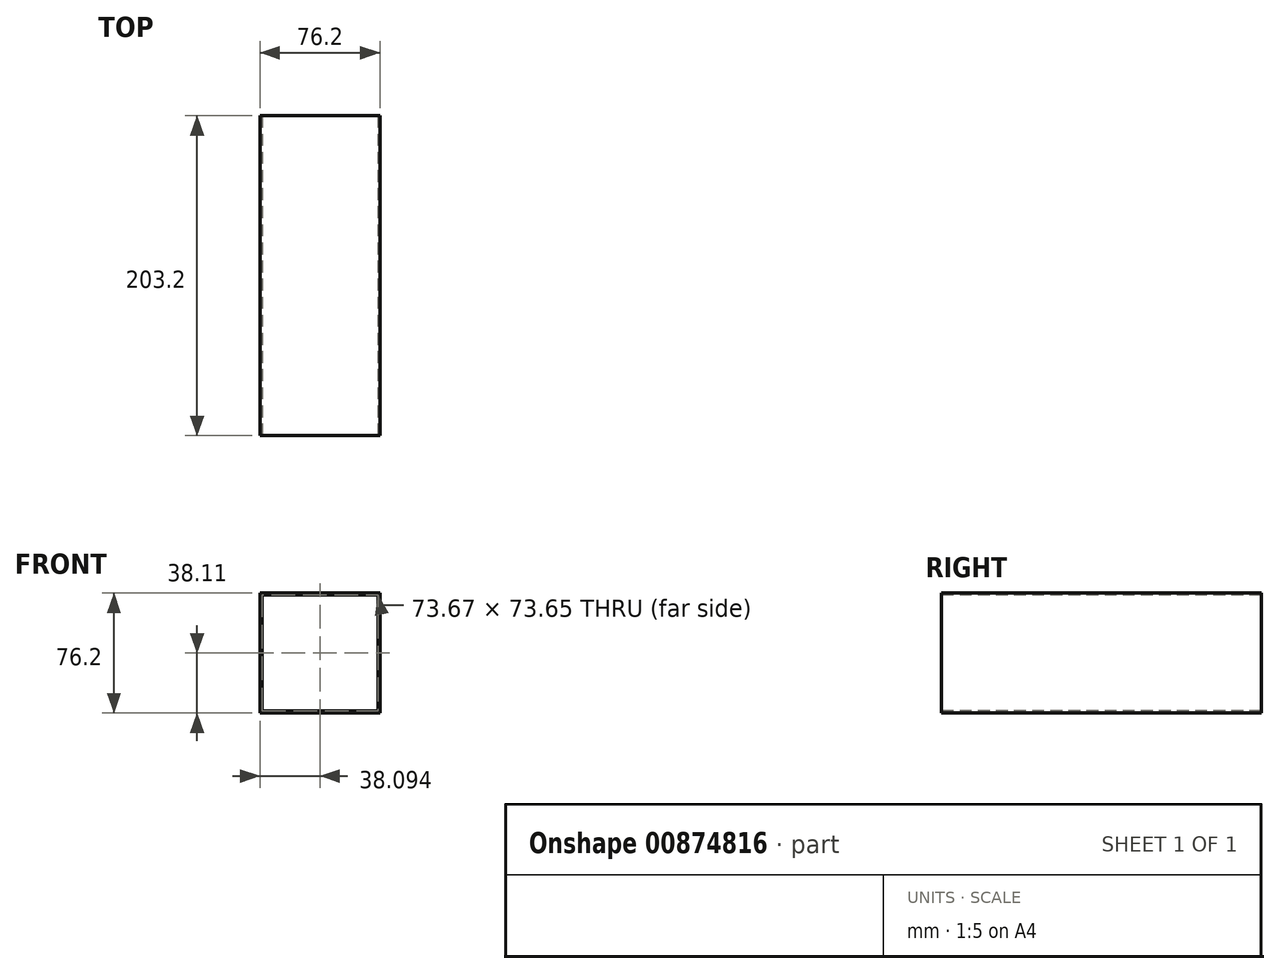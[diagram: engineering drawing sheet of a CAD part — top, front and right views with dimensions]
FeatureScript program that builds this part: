
annotation { "Feature Type Name" : "Feature", "Feature Type Description" : "" }
export const myFeature = defineFeature(function(context is Context, id is Id, definition is map)
    precondition{}
    {
        {
            var Q0;
            Q0=qCreatedBy(makeId("Front.planeOp"),FACE);
            var sketch = newSketch(context, id + "F0", { "sketchPlane" : qUnion([Q0])});
            skLineSegment(sketch, "E0.bottom", {"start": v(-117.25, 89.57) * mm, "end": v(-41.05, 89.57) * mm});
            skLineSegment(sketch, "E0.top", {"start": v(-117.25, 13.37) * mm, "end": v(-41.05, 13.37) * mm});
            skLineSegment(sketch, "E0.left", {"start": v(-117.25, 89.57) * mm, "end": v(-117.25, 13.37) * mm});
            skLineSegment(sketch, "E0.right", {"start": v(-41.05, 89.57) * mm, "end": v(-41.05, 13.37) * mm});
            skSolve(sketch);
        }
        {
            var Q0;
            Q0=qSketchRegion(id+"F0",true);
            extrude(context, id + "F1", {"entities" : qUnion([Q0]), "depth" : 609.6 * mm, "offsetDistance" : 25.4 * mm});
        }
        {
            var Q0;
            Q0=makeQuery(id+"F1.opExtrude","CAP_FACE",FACE,{"disambiguationData":[OSD([sQuery(id+"F0.wireOp",EDGE,"E0.bottom"),sQuery(id+"F0.wireOp",EDGE,"E0.top"),sQuery(id+"F0.wireOp",EDGE,"E0.left"),sQuery(id+"F0.wireOp",EDGE,"E0.right")])],"isStart":false});
            var sketch = newSketch(context, id + "F2", { "sketchPlane" : qUnion([Q0])});
            skLineSegment(sketch, "E1", {"start": v(-98.69, 89.57) * mm, "end": v(-98.69, 88.3) * mm});
            skLineSegment(sketch, "E2", {"start": v(-98.69, 88.3) * mm, "end": v(-116, 88.3) * mm});
            skLineSegment(sketch, "E3", {"start": v(-116, 88.3) * mm, "end": v(-116, 14.66) * mm});
            skLineSegment(sketch, "E4", {"start": v(-116, 14.66) * mm, "end": v(-42.32, 14.66) * mm});
            skLineSegment(sketch, "E5", {"start": v(-42.32, 14.66) * mm, "end": v(-42.32, 88.3) * mm});
            skLineSegment(sketch, "E6", {"start": v(-42.32, 88.3) * mm, "end": v(-98.69, 88.3) * mm});
            skSolve(sketch);
        }
        {
            var Q0;
            Q0=makeQuery(id+"F2.imprint","IMPRINT",FACE,{"disambiguationData":[TD([[makeQuery(id+"F2.imprint","IMPRINT",EDGE,{"derivedFrom":sQuery(id+"F2.wireOp",EDGE,"E2")}),1.0]])]});
            extrude(context, id + "F3", {"entities" : qUnion([Q0]), "operationType" : NewBodyOperationType.REMOVE, "oppositeDirection" : true, "depth" : 914.4 * mm, "offsetDistance" : 25.4 * mm});
        }
        {
            var Q0;
            Q0=makeQuery(id+"F1.opExtrude","CAP_FACE",FACE,{"disambiguationData":[OSD([sQuery(id+"F0.wireOp",EDGE,"E0.bottom"),sQuery(id+"F0.wireOp",EDGE,"E0.top"),sQuery(id+"F0.wireOp",EDGE,"E0.left"),sQuery(id+"F0.wireOp",EDGE,"E0.right")])],"isStart":false});
            extrude(context, id + "F4", {"entities" : qUnion([Q0]), "operationType" : NewBodyOperationType.ADD, "depth" : 304.8 * mm, "offsetDistance" : 25.4 * mm});
        }
        {
            var Q0;
            Q0=makeQuery(id+"F1.opExtrude","CAP_FACE",FACE,{"disambiguationData":[OSD([sQuery(id+"F0.wireOp",EDGE,"E0.bottom"),sQuery(id+"F0.wireOp",EDGE,"E0.top"),sQuery(id+"F0.wireOp",EDGE,"E0.left"),sQuery(id+"F0.wireOp",EDGE,"E0.right")])],"isStart":true});
            extrude(context, id + "F5", {"entities" : qUnion([Q0]), "operationType" : NewBodyOperationType.REMOVE, "oppositeDirection" : true, "depth" : 508 * mm, "offsetDistance" : 25.4 * mm});
        }
        {
            var Q0;
            Q0=makeQuery(id+"F5.boolean.opBoolean","COPY",FACE,{"derivedFrom":makeQuery(id+"F5.opExtrude","CAP_FACE",FACE,{"disambiguationData":[OSD([sQuery(id+"F0.wireOp",EDGE,"E0.bottom"),sQuery(id+"F0.wireOp",EDGE,"E0.top"),sQuery(id+"F0.wireOp",EDGE,"E0.left"),sQuery(id+"F0.wireOp",EDGE,"E0.right")])],"isStart":false})});
            extrude(context, id + "F6", {"entities" : qUnion([Q0]), "operationType" : NewBodyOperationType.REMOVE, "oppositeDirection" : true, "depth" : 381 * mm, "offsetDistance" : 25.4 * mm});
        }
        {
            var Q0;
            Q0=makeQuery(id+"F6.boolean.opBoolean","COPY",FACE,{"derivedFrom":makeQuery(id+"F6.opExtrude","CAP_FACE",FACE,{"disambiguationData":[OSD([sQuery(id+"F0.wireOp",EDGE,"E0.bottom"),sQuery(id+"F0.wireOp",EDGE,"E0.top"),sQuery(id+"F0.wireOp",EDGE,"E0.left"),sQuery(id+"F0.wireOp",EDGE,"E0.right")])],"isStart":false})});
            extrude(context, id + "F7", {"entities" : qUnion([Q0]), "operationType" : NewBodyOperationType.ADD, "depth" : 177.8 * mm, "offsetDistance" : 25.4 * mm});
        }
    });
